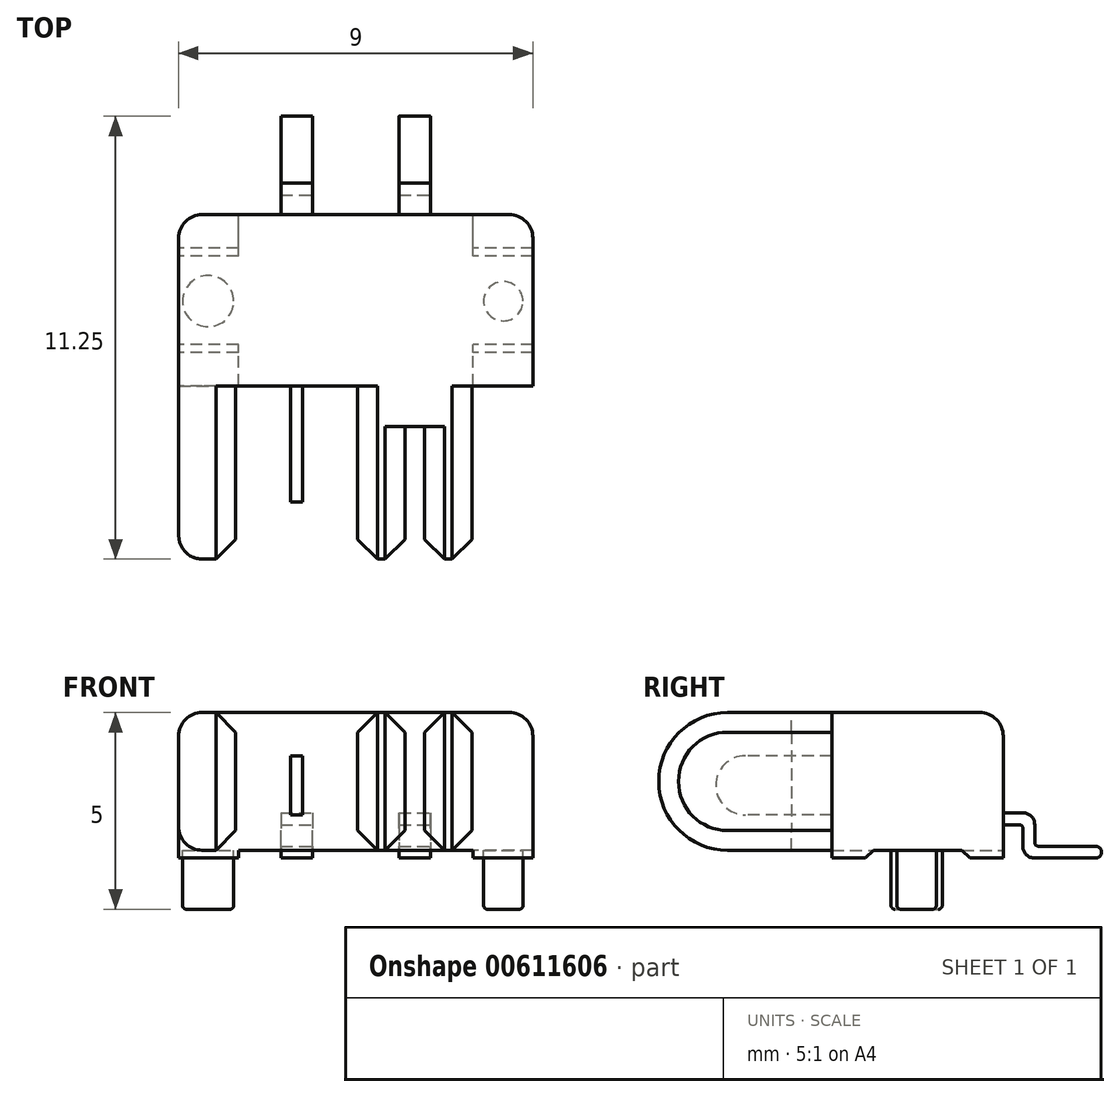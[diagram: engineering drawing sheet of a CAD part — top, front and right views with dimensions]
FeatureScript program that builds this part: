
annotation { "Feature Type Name" : "Feature", "Feature Type Description" : "" }
export const myFeature = defineFeature(function(context is Context, id is Id, definition is map)
    precondition{}
    {
        {
            var Q0;
            Q0=qCreatedBy(makeId("Top.planeOp"),FACE);
            var sketch = newSketch(context, id + "F0", { "sketchPlane" : qUnion([Q0])});
            skLineSegment(sketch, "E0.bottom", {"start": v(-11.54, 11.3) * mm, "end": v(-2.54, 11.3) * mm});
            skLineSegment(sketch, "E0.top", {"start": v(-11.54, 2.54) * mm, "end": v(-10.1, 2.54) * mm});
            skLineSegment(sketch, "E0.left", {"start": v(-11.54, 11.3) * mm, "end": v(-11.54, 2.54) * mm});
            skLineSegment(sketch, "E0.right", {"start": v(-2.54, 11.3) * mm, "end": v(-2.54, 6.94) * mm});
            skLineSegment(sketch, "E1", {"start": v(-10.1, 2.54) * mm, "end": v(-10.1, 6.94) * mm});
            skLineSegment(sketch, "E2", {"start": v(-10.1, 6.94) * mm, "end": v(-8.7, 6.94) * mm});
            skLineSegment(sketch, "E3", {"start": v(-5.8, 2.54) * mm, "end": v(-5.8, 5.9) * mm});
            skLineSegment(sketch, "E4", {"start": v(-5.8, 5.9) * mm, "end": v(-5.3, 5.9) * mm});
            skLineSegment(sketch, "E5", {"start": v(-5.3, 5.9) * mm, "end": v(-5.3, 2.54) * mm});
            skLineSegment(sketch, "E6", {"start": v(-4.1, 2.54) * mm, "end": v(-4.1, 6.94) * mm});
            skLineSegment(sketch, "E7", {"start": v(-4.1, 6.94) * mm, "end": v(-2.54, 6.94) * mm});
            skLineSegment(sketch, "E8.trimOffspring", {"start": v(-5.3, 2.54) * mm, "end": v(-4.1, 2.54) * mm});
            skLineSegment(sketch, "E9.top", {"start": v(-8.7, 4) * mm, "end": v(-8.4, 4) * mm});
            skLineSegment(sketch, "E9.left", {"start": v(-8.7, 6.94) * mm, "end": v(-8.7, 4) * mm});
            skLineSegment(sketch, "E9.right", {"start": v(-8.4, 6.94) * mm, "end": v(-8.4, 4) * mm});
            skLineSegment(sketch, "E10", {"start": v(-8.54, 4) * mm, "end": v(-8.54, 14.3) * mm, "construction": true});
            skLineSegment(sketch, "E11", {"start": v(-5.54, 2.03) * mm, "end": v(-5.54, 14.3) * mm, "construction": true});
            skLineSegment(sketch, "E12", {"start": v(-8.4, 6.94) * mm, "end": v(-7, 6.94) * mm});
            skLineSegment(sketch, "E13", {"start": v(-7, 6.94) * mm, "end": v(-7, 2.54) * mm});
            skLineSegment(sketch, "E14", {"start": v(-5.8, 2.54) * mm, "end": v(-7, 2.54) * mm});
            skSolve(sketch);
        }
        {
            var Q0;
            Q0 = qSketchRegion(id + "F0", true);
            extrude(context, id + "F1", {"entities" : qUnion([Q0]), "depth" : 3.7 * mm, "offsetDistance" : 25 * mm});
        }
        {
            var Q0;
            Q0=makeQuery(id+"F1.opExtrude","SWEPT_FACE",FACE,{"disambiguationData":[OSD([sQuery(id+"F0.wireOp",EDGE,"E0.left")])]});
            var sketch = newSketch(context, id + "F2", { "sketchPlane" : qUnion([Q0])});
            skArc(sketch, "E15", {"start": v(-4.29, 0.2) * mm, "mid": v(-2.54, 1.95) * mm, "end": v(-4.29, 3.7) * mm});
            skPoint(sketch, "E15.second.point", {"position": v(-4.29, 3.7) * mm});
            skPoint(sketch, "E15.third.point", {"position": v(-4.29, 0.2) * mm});
            skLineSegment(sketch, "E16", {"start": v(-6.94, 0.2) * mm, "end": v(-4.29, 0.2) * mm});
            skLineSegment(sketch, "E17", {"start": v(-6.94, 0.2) * mm, "end": v(-6.94, 0) * mm});
            skLineSegment(sketch, "E18", {"start": v(-6.94, 0) * mm, "end": v(-2.54, 0) * mm});
            skLineSegment(sketch, "E19", {"start": v(-2.54, 3.7) * mm, "end": v(-4.29, 3.7) * mm});
            skLineSegment(sketch, "E20", {"start": v(-2.54, 3.7) * mm, "end": v(-2.54, 0) * mm});
            skSolve(sketch);
        }
        {
            var Q0;
            Q0 = qSketchRegion(id + "F2", true);
            extrude(context, id + "F3", {"entities" : qUnion([Q0]), "operationType" : NewBodyOperationType.REMOVE, "oppositeDirection" : true, "depth" : 9 * mm, "offsetDistance" : 25 * mm});
        }
        {
            var Q0;
            Q0=makeQuery(id+"F1.opExtrude","SWEPT_FACE",FACE,{"disambiguationData":[OSD([sQuery(id+"F0.wireOp",EDGE,"E9.top")])]});
            var sketch = newSketch(context, id + "F4", { "sketchPlane" : qUnion([Q0])});
            skLineSegment(sketch, "E21.bottom", {"start": v(-8.7, 2.6) * mm, "end": v(-8.4, 2.6) * mm});
            skLineSegment(sketch, "E21.top", {"start": v(-8.7, 3.7) * mm, "end": v(-8.4, 3.7) * mm});
            skLineSegment(sketch, "E21.left", {"start": v(-8.7, 2.6) * mm, "end": v(-8.7, 3.7) * mm});
            skLineSegment(sketch, "E21.right", {"start": v(-8.4, 2.6) * mm, "end": v(-8.4, 3.7) * mm});
            skLineSegment(sketch, "E22.bottom", {"start": v(-8.7, 1.1) * mm, "end": v(-8.4, 1.1) * mm});
            skLineSegment(sketch, "E22.top", {"start": v(-8.7, 0) * mm, "end": v(-8.4, 0) * mm});
            skLineSegment(sketch, "E22.left", {"start": v(-8.7, 1.1) * mm, "end": v(-8.7, 0) * mm});
            skLineSegment(sketch, "E22.right", {"start": v(-8.4, 1.1) * mm, "end": v(-8.4, 0) * mm});
            skSolve(sketch);
        }
        {
            var Q0;
            Q0 = qSketchRegion(id + "F4", true);
            extrude(context, id + "F5", {"entities" : qUnion([Q0]), "operationType" : NewBodyOperationType.REMOVE, "oppositeDirection" : true, "depth" : 2.95 * mm, "offsetDistance" : 25 * mm});
        }
        {
            var Q0;
            Q0=makeQuery(id+"F1.opExtrude","SWEPT_FACE",FACE,{"disambiguationData":[OSD([sQuery(id+"F0.wireOp",EDGE,"E9.right")])]});
            var sketch = newSketch(context, id + "F6", { "sketchPlane" : qUnion([Q0])});
            skArc(sketch, "E23", {"start": v(4.74, 2.6) * mm, "mid": v(4, 1.85) * mm, "end": v(4.74, 1.1) * mm});
            skPoint(sketch, "E23.first.point", {"position": v(4, 1.85) * mm});
            skPoint(sketch, "E23.second.point", {"position": v(4.74, 2.6) * mm});
            skPoint(sketch, "E23.third.point", {"position": v(4.74, 1.1) * mm});
            skLineSegment(sketch, "E24", {"start": v(4.74, 1.1) * mm, "end": v(4, 1.1) * mm});
            skLineSegment(sketch, "E25", {"start": v(4, 1.1) * mm, "end": v(4, 1.85) * mm});
            skLineSegment(sketch, "E26", {"start": v(4, 1.85) * mm, "end": v(4, 2.6) * mm});
            skLineSegment(sketch, "E27", {"start": v(4, 2.6) * mm, "end": v(4.74, 2.6) * mm});
            skSolve(sketch);
        }
        {
            var Q0;
            Q0 = qSketchRegion(id + "F6", true);
            extrude(context, id + "F7", {"entities" : qUnion([Q0]), "operationType" : NewBodyOperationType.REMOVE, "endBound" : BoundingType.UP_TO_NEXT, "oppositeDirection" : true, "depth" : 25 * mm, "offsetDistance" : 25 * mm});
        }
        {
            var Q0;
            Q0=qCreatedBy(makeId("Top.planeOp"),FACE);
            var sketch = newSketch(context, id + "F8", { "sketchPlane" : qUnion([Q0])});
            skLineSegment(sketch, "E28.bottom", {"start": v(-8.94, 11.3) * mm, "end": v(-8.14, 11.3) * mm});
            skLineSegment(sketch, "E28.top", {"start": v(-8.94, 13.8) * mm, "end": v(-8.14, 13.8) * mm});
            skLineSegment(sketch, "E28.left", {"start": v(-8.94, 11.3) * mm, "end": v(-8.94, 13.8) * mm});
            skLineSegment(sketch, "E28.right", {"start": v(-8.14, 11.3) * mm, "end": v(-8.14, 13.8) * mm});
            skLineSegment(sketch, "E29.bottom", {"start": v(-5.14, 13.8) * mm, "end": v(-5.94, 13.8) * mm});
            skLineSegment(sketch, "E29.top", {"start": v(-5.14, 11.3) * mm, "end": v(-5.94, 11.3) * mm});
            skLineSegment(sketch, "E29.left", {"start": v(-5.14, 13.8) * mm, "end": v(-5.14, 11.3) * mm});
            skLineSegment(sketch, "E29.right", {"start": v(-5.94, 13.8) * mm, "end": v(-5.94, 11.3) * mm});
            skSolve(sketch);
        }
        {
            var Q0;
            Q0 = qSketchRegion(id + "F8", true);
            extrude(context, id + "F9", {"entities" : qUnion([Q0]), "operationType" : NewBodyOperationType.ADD, "depth" : 1.5 * mm, "offsetDistance" : 25 * mm});
        }
        {
            var Q0;
            Q0=makeQuery(id+"F9.opExtrude","SWEPT_FACE",FACE,{"disambiguationData":[OSD([sQuery(id+"F8.wireOp",EDGE,"E29.left")])]});
            var sketch = newSketch(context, id + "F10", { "sketchPlane" : qUnion([Q0])});
            skLineSegment(sketch, "E30", {"start": v(11.3, 1.15) * mm, "end": v(11.8, 1.15) * mm});
            skLineSegment(sketch, "E31", {"start": v(12.1, 0.85) * mm, "end": v(12.1, 0.4) * mm});
            skLineSegment(sketch, "E32", {"start": v(12.2, 0.3) * mm, "end": v(13.8, 0.3) * mm});
            skLineSegment(sketch, "E33", {"start": v(13.8, 0.3) * mm, "end": v(13.8, 1.5) * mm});
            skLineSegment(sketch, "E34", {"start": v(13.8, 1.5) * mm, "end": v(11.3, 1.5) * mm});
            skLineSegment(sketch, "E35", {"start": v(11.3, 1.5) * mm, "end": v(11.3, 1.15) * mm});
            skLineSegment(sketch, "E36", {"start": v(11.3, 0.85) * mm, "end": v(11.7, 0.85) * mm});
            skLineSegment(sketch, "E37", {"start": v(11.8, 0.75) * mm, "end": v(11.8, 0.3) * mm});
            skLineSegment(sketch, "E38", {"start": v(11.3, 0) * mm, "end": v(11.3, 0.85) * mm});
            skPoint(sketch, "E39.visualSharp", {"position": v(12.1, 0.3) * mm});
            skArc(sketch, "E39.filletArc", {"start": v(12.1, 0.4) * mm, "mid": v(12.12, 0.33) * mm, "end": v(12.2, 0.3) * mm});
            skPoint(sketch, "E40.visualSharp", {"position": v(12.1, 1.15) * mm});
            skArc(sketch, "E40.filletArc", {"start": v(12.1, 0.85) * mm, "mid": v(12, 1.06) * mm, "end": v(11.8, 1.15) * mm});
            skArc(sketch, "E41.filletArc", {"start": v(11.8, 0.75) * mm, "mid": v(11.76, 0.82) * mm, "end": v(11.7, 0.85) * mm});
            skArc(sketch, "E42", {"start": v(11.8, 0.3) * mm, "mid": v(11.88, 0.09) * mm, "end": v(12.1, 0) * mm});
            skLineSegment(sketch, "E43", {"start": v(12.1, 0) * mm, "end": v(11.3, 0) * mm});
            skArc(sketch, "E44", {"start": v(13.64, 0) * mm, "mid": v(13.8, 0.15) * mm, "end": v(13.64, 0.3) * mm});
            skLineSegment(sketch, "E45", {"start": v(13.8, 0) * mm, "end": v(13.64, 0) * mm});
            skLineSegment(sketch, "E46", {"start": v(13.8, 0.3) * mm, "end": v(13.8, 0) * mm});
            skSolve(sketch);
        }
        {
            var Q0;
            Q0 = qSketchRegion(id + "F10", true);
            extrude(context, id + "F11", {"entities" : qUnion([Q0]), "operationType" : NewBodyOperationType.REMOVE, "oppositeDirection" : true, "depth" : 9 * mm, "offsetDistance" : 25 * mm});
        }
        {
            var Q0;
            Q0=makeQuery(id+"F1.opExtrude","CAP_EDGE",EDGE,{"disambiguationData":[OSD([sQuery(id+"F0.wireOp",EDGE,"E0.bottom")])],"isStart":false});
            var Q1;
            Q1=makeQuery(id+"F1.opExtrude","CAP_EDGE",EDGE,{"disambiguationData":[OSD([sQuery(id+"F0.wireOp",EDGE,"E0.left")])],"isStart":false});
            var Q2;
            Q2=makeQuery(id+"F11.boolean.opBoolean","INTERSECT",EDGE,{"derivedFrom":[makeQuery(id+"F11.opExtrude","SWEPT_FACE",FACE,{"disambiguationData":[OSD([sQuery(id+"F10.wireOp",EDGE,"E35")])]}),makeQuery(id+"F11.opExtrude","SWEPT_FACE",FACE,{"disambiguationData":[OSD([sQuery(id+"F10.wireOp",EDGE,"E38")])]})]});
            var Q3;
            Q3=makeQuery(id+"F1.opExtrude","CAP_EDGE",EDGE,{"disambiguationData":[OSD([sQuery(id+"F0.wireOp",EDGE,"E0.right")])],"isStart":false});
            var Q4;
            Q4=makeQuery(id+"F1.opExtrude","SWEPT_EDGE",EDGE,{"disambiguationData":[OSD([sQuery(id+"F0.wireOp",EDGE,"E0.bottom"),sQuery(id+"F0.wireOp",EDGE,"E0.right")])]});
            fillet(context, id + "F12", {"entities" : qUnion([Q0, Q1, Q2, Q3, Q4]), "radius" : .6 * mm, "tangentPropagation" : true, "allowEdgeOverflow" : false});
        }
        {
            var Q0;
            Q0=makeQuery(id+"F1.opExtrude","CAP_EDGE",EDGE,{"disambiguationData":[OSD([sQuery(id+"F0.wireOp",EDGE,"E13")])],"isStart":false});
            var Q1;
            {var subQ0=sQuery(id+"F2.wireOp",EDGE,"E15");var subQ1=makeQuery(id+"F2.imprint","INTERSECT",VERTEX,{"derivedFrom":[subQ0,sQuery(id+"F2.wireOp",EDGE,"E20")]});Q1=makeQuery(id+"F3.boolean.opBoolean","INTERSECT",EDGE,{"derivedFrom":[makeQuery(id+"F1.opExtrude","SWEPT_FACE",FACE,{"disambiguationData":[OSD([sQuery(id+"F0.wireOp",EDGE,"E1")])]}),makeQuery(id+"F3.opExtrude","SWEPT_FACE",FACE,{"disambiguationData":[OSD([subQ0]),TDD([makeQuery(id+"F2.imprint","IMPRINT",EDGE,{"disambiguationData":[TD([[makeQuery(id+"F2.imprint","INTERSECT",VERTEX,{"derivedFrom":[subQ0,sQuery(id+"F2.wireOp",EDGE,"E16")]}),-1.0]])],"derivedFrom":subQ0})])]}),makeQuery(id+"F3.opExtrude","SWEPT_FACE",FACE,{"disambiguationData":[OSD([subQ0]),TDD([makeQuery(id+"F2.imprint","IMPRINT",EDGE,{"disambiguationData":[TD([[subQ1,-1.0]])],"derivedFrom":subQ0})])]})]});}
            var Q2;
            {var subQ0=sQuery(id+"F2.wireOp",EDGE,"E15");var subQ1=makeQuery(id+"F2.imprint","INTERSECT",VERTEX,{"derivedFrom":[subQ0,sQuery(id+"F2.wireOp",EDGE,"E20")]});Q2=makeQuery(id+"F3.boolean.opBoolean","INTERSECT",EDGE,{"derivedFrom":[makeQuery(id+"F1.opExtrude","SWEPT_FACE",FACE,{"disambiguationData":[OSD([sQuery(id+"F0.wireOp",EDGE,"E5")])]}),makeQuery(id+"F3.opExtrude","SWEPT_FACE",FACE,{"disambiguationData":[OSD([subQ0]),TDD([makeQuery(id+"F2.imprint","IMPRINT",EDGE,{"disambiguationData":[TD([[makeQuery(id+"F2.imprint","INTERSECT",VERTEX,{"derivedFrom":[subQ0,sQuery(id+"F2.wireOp",EDGE,"E16")]}),-1.0]])],"derivedFrom":subQ0})])]}),makeQuery(id+"F3.opExtrude","SWEPT_FACE",FACE,{"disambiguationData":[OSD([subQ0]),TDD([makeQuery(id+"F2.imprint","IMPRINT",EDGE,{"disambiguationData":[TD([[subQ1,-1.0]])],"derivedFrom":subQ0})])]})]});}
            var Q3;
            {var subQ0=sQuery(id+"F2.wireOp",EDGE,"E15");var subQ1=makeQuery(id+"F2.imprint","INTERSECT",VERTEX,{"derivedFrom":[subQ0,sQuery(id+"F2.wireOp",EDGE,"E20")]});Q3=makeQuery(id+"F3.boolean.opBoolean","INTERSECT",EDGE,{"derivedFrom":[makeQuery(id+"F1.opExtrude","SWEPT_FACE",FACE,{"disambiguationData":[OSD([sQuery(id+"F0.wireOp",EDGE,"E6")])]}),makeQuery(id+"F3.opExtrude","SWEPT_FACE",FACE,{"disambiguationData":[OSD([subQ0]),TDD([makeQuery(id+"F2.imprint","IMPRINT",EDGE,{"disambiguationData":[TD([[makeQuery(id+"F2.imprint","INTERSECT",VERTEX,{"derivedFrom":[subQ0,sQuery(id+"F2.wireOp",EDGE,"E16")]}),-1.0]])],"derivedFrom":subQ0})])]}),makeQuery(id+"F3.opExtrude","SWEPT_FACE",FACE,{"disambiguationData":[OSD([subQ0]),TDD([makeQuery(id+"F2.imprint","IMPRINT",EDGE,{"disambiguationData":[TD([[subQ1,-1.0]])],"derivedFrom":subQ0})])]})]});}
            var Q4;
            {var subQ0=sQuery(id+"F2.wireOp",EDGE,"E15");var subQ1=makeQuery(id+"F2.imprint","INTERSECT",VERTEX,{"derivedFrom":[subQ0,sQuery(id+"F2.wireOp",EDGE,"E20")]});Q4=makeQuery(id+"F3.boolean.opBoolean","INTERSECT",EDGE,{"derivedFrom":[makeQuery(id+"F1.opExtrude","SWEPT_FACE",FACE,{"disambiguationData":[OSD([sQuery(id+"F0.wireOp",EDGE,"E3")])]}),makeQuery(id+"F3.opExtrude","SWEPT_FACE",FACE,{"disambiguationData":[OSD([subQ0]),TDD([makeQuery(id+"F2.imprint","IMPRINT",EDGE,{"disambiguationData":[TD([[makeQuery(id+"F2.imprint","INTERSECT",VERTEX,{"derivedFrom":[subQ0,sQuery(id+"F2.wireOp",EDGE,"E16")]}),-1.0]])],"derivedFrom":subQ0})])]}),makeQuery(id+"F3.opExtrude","SWEPT_FACE",FACE,{"disambiguationData":[OSD([subQ0]),TDD([makeQuery(id+"F2.imprint","IMPRINT",EDGE,{"disambiguationData":[TD([[subQ1,-1.0]])],"derivedFrom":subQ0})])]})]});}
            chamfer(context, id + "F13", {"entities" : qUnion([Q0, Q1, Q2, Q3, Q4]), "width" : .5 * mm, "tangentPropagation" : true});
        }
        {
            var Q0;
            Q0=makeQuery(id+"F1.opExtrude","SWEPT_FACE",FACE,{"disambiguationData":[OSD([sQuery(id+"F0.wireOp",EDGE,"E0.left")])]});
            var sketch = newSketch(context, id + "F14", { "sketchPlane" : qUnion([Q0])});
            skLineSegment(sketch, "E47", {"start": v(-10.44, 0) * mm, "end": v(-10.24, 0.2) * mm});
            skLineSegment(sketch, "E48", {"start": v(-10.24, 0.2) * mm, "end": v(-8, 0.2) * mm});
            skLineSegment(sketch, "E49", {"start": v(-8, 0.2) * mm, "end": v(-7.8, 0) * mm});
            skLineSegment(sketch, "E50", {"start": v(-7.8, 0) * mm, "end": v(-10.44, 0) * mm});
            skSolve(sketch);
        }
        {
            var Q0;
            Q0 = qSketchRegion(id + "F14", true);
            extrude(context, id + "F15", {"entities" : qUnion([Q0]), "operationType" : NewBodyOperationType.REMOVE, "endBound" : BoundingType.UP_TO_NEXT, "oppositeDirection" : true, "depth" : 25 * mm, "offsetDistance" : 25 * mm});
        }
        {
            var Q0;
            Q0=makeQuery(id+"F11.boolean.opBoolean","MERGE",FACE,{"derivedFrom":[makeQuery(id+"F1.opExtrude","SWEPT_FACE",FACE,{"disambiguationData":[OSD([sQuery(id+"F0.wireOp",EDGE,"E0.bottom")])]}),makeQuery(id+"F11.opExtrude","SWEPT_FACE",FACE,{"disambiguationData":[OSD([sQuery(id+"F10.wireOp",EDGE,"E35")])]}),makeQuery(id+"F11.opExtrude","SWEPT_FACE",FACE,{"disambiguationData":[OSD([sQuery(id+"F10.wireOp",EDGE,"E38")])]})]});
            var sketch = newSketch(context, id + "F16", { "sketchPlane" : qUnion([Q0])});
            skLineSegment(sketch, "E51.bottom", {"start": v(4.06, 0) * mm, "end": v(10.02, 0) * mm});
            skLineSegment(sketch, "E51.top", {"start": v(4.06, 0.2) * mm, "end": v(10.02, 0.2) * mm});
            skLineSegment(sketch, "E51.left", {"start": v(4.06, 0) * mm, "end": v(4.06, 0.2) * mm});
            skLineSegment(sketch, "E51.right", {"start": v(10.02, 0) * mm, "end": v(10.02, 0.2) * mm});
            skSolve(sketch);
        }
        {
            var Q0;
            Q0 = qSketchRegion(id + "F16", true);
            extrude(context, id + "F17", {"entities" : qUnion([Q0]), "operationType" : NewBodyOperationType.REMOVE, "oppositeDirection" : true, "depth" : 4.35 * mm, "offsetDistance" : 25 * mm});
        }
        {
            var Q0;
            {var subQ2=sQuery(id+"F2.wireOp",EDGE,"E16");Q0=makeQuery(id+"F17.boolean.opBoolean","MERGE",FACE,{"derivedFrom":[makeQuery(id+"F3.boolean.opBoolean","COPY",FACE,{"disambiguationData":[TD([makeQuery(id+"F1.opExtrude","SWEPT_FACE",FACE,{"disambiguationData":[OSD([sQuery(id+"F0.wireOp",EDGE,"E3")])]})])],"derivedFrom":makeQuery(id+"F3.opExtrude","SWEPT_FACE",FACE,{"disambiguationData":[OSD([subQ2])]})}),makeQuery(id+"F15.boolean.opBoolean","COPY",FACE,{"derivedFrom":makeQuery(id+"F15.opExtrude","SWEPT_FACE",FACE,{"disambiguationData":[OSD([sQuery(id+"F14.wireOp",EDGE,"E48")])]})}),makeQuery(id+"F17.opExtrude","SWEPT_FACE",FACE,{"disambiguationData":[OSD([sQuery(id+"F16.wireOp",EDGE,"E51.top")])]})]});}
            var sketch = newSketch(context, id + "F18", { "sketchPlane" : qUnion([Q0])});
            skCircle(sketch, "E52", {"center": v(-10.79, -9.1) * mm, "radius": 0.65 * mm});
            skCircle(sketch, "E53", {"center": v(-3.29, -9.1) * mm, "radius": 0.5 * mm});
            skSolve(sketch);
        }
        {
            var Q0;
            Q0 = qSketchRegion(id + "F18", true);
            extrude(context, id + "F19", {"entities" : qUnion([Q0]), "operationType" : NewBodyOperationType.ADD, "depth" : 1.5 * mm, "offsetDistance" : 25 * mm});
        }
        {
            var Q0;
            Q0=makeQuery(id+"F19.opExtrude","CAP_EDGE",EDGE,{"disambiguationData":[OSD([sQuery(id+"F18.wireOp",EDGE,"E53")])],"isStart":false});
            var Q1;
            Q1=makeQuery(id+"F19.opExtrude","CAP_EDGE",EDGE,{"disambiguationData":[OSD([sQuery(id+"F18.wireOp",EDGE,"E52")])],"isStart":false});
            fillet(context, id + "F20", {"entities" : qUnion([Q0, Q1]), "radius" : .1 * mm, "tangentPropagation" : true, "allowEdgeOverflow" : false});
        }
    });
